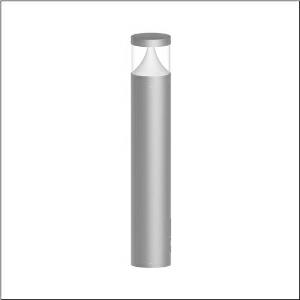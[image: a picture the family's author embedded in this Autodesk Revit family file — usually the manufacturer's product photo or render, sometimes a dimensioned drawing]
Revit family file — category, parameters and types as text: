
# Revit family: cl_31_poller_90_5cl444603
name_source: partatom
category: Lighting Fixtures
units: mm (PartAtom-declared; Revit-internal decimal feet)

## family parameters
Cut with Voids When Loaded = No
Host = Face
Light Source = No
Part Type = Normal
Room Calculation Point = No
Round Connector Dimension = Use Diameter
Shared = No

## types (1)
- --- (1 x LED, 1500 lm, 14 W, 3000K)
    Apparent Load = 14 VA
    CIE Flux Codes = 19 66 88 92 100
    Color Rendering = 80
    Color Temperature = 3000K
    Default Elevation = 1800 mm
    Description = CL 31 Bollard 90, bollard luminaire, primary light control with lens, of PC, primary optical cover: cover panel, of PC, transparent, secondary light control with reflector, of PC, primary light characteristic: asymmetric, LED, rated luminous flux: 1.500lm, luminous efficacy: 107lm/W, light colour: 830, colour temperature: 3000K, control gear: ECG DALI, with terminal, 5-pole, max. 2.5mm², mains connection: 220..240V, AC, 50/60Hz, rated input power: 14W, luminaire housing, of aluminium, powder-coated, Siteco® metallic grey, diameter: 170mm, height: 900mm, protection rating (complete): IP65, insulation class (complete): insulation class I (protective earthing), certification: CE, ENEC, impact resistance: IK10, permissible operating ambient temperature for outdoor applications: -20..+50°C, packaging unit: 1 piece
    Height = 200 mm  [stored 0.656168 ft]
    Lamp = 1 x LED
    Lamp Light Flux = 1500 lm
    Lamp Power = 14 W
    Lamp count = 1
    Length = 170 mm  [stored 0.557743 ft]
    Luminous efficacy = 107 lm/W
    Manufacturer = Siteco
    ModVariant = No
    Model = 5CL444603
    Mounting Place = Floor
    Mounting Type = Freestanding
    Number of Poles = 1
    OnlyDefault = Yes
    Power Factor = 1
    Product Name = CL 31 Poller 90
    Product group = bollard luminaire | freestanding
    ProductGroupID = 1303
    Protection Class = Protection class I
    Protection Degree = IP 65
    RLX_Detail_Level = 1
    RlxData = <blob elided: 64789 chars, md5=5a88d47b>
    Socket = socket
    Standby Power = 0 W
    System Light Flux = 1500 lm
    System Power = 14 W
    Type Comments = factory setting: luminous flux: 100 % | dim-lin: 254 | 350 mA
    Type Image = l_1006899.jpg
    URL = http://relux.com
    VarID = @adj_116969
    Voltage = 0 V
    Weight = 0.00 kg
    Width = 0 mm  [stored 0 ft]

note: [stored X ft] marks values corroborated as IEEE doubles in the binary element streams (Revit-internal decimal feet)

## geometry (parser evidence)
native form markers: Blend x4, Sweep x8
no freeform markers — native parametric forms only
